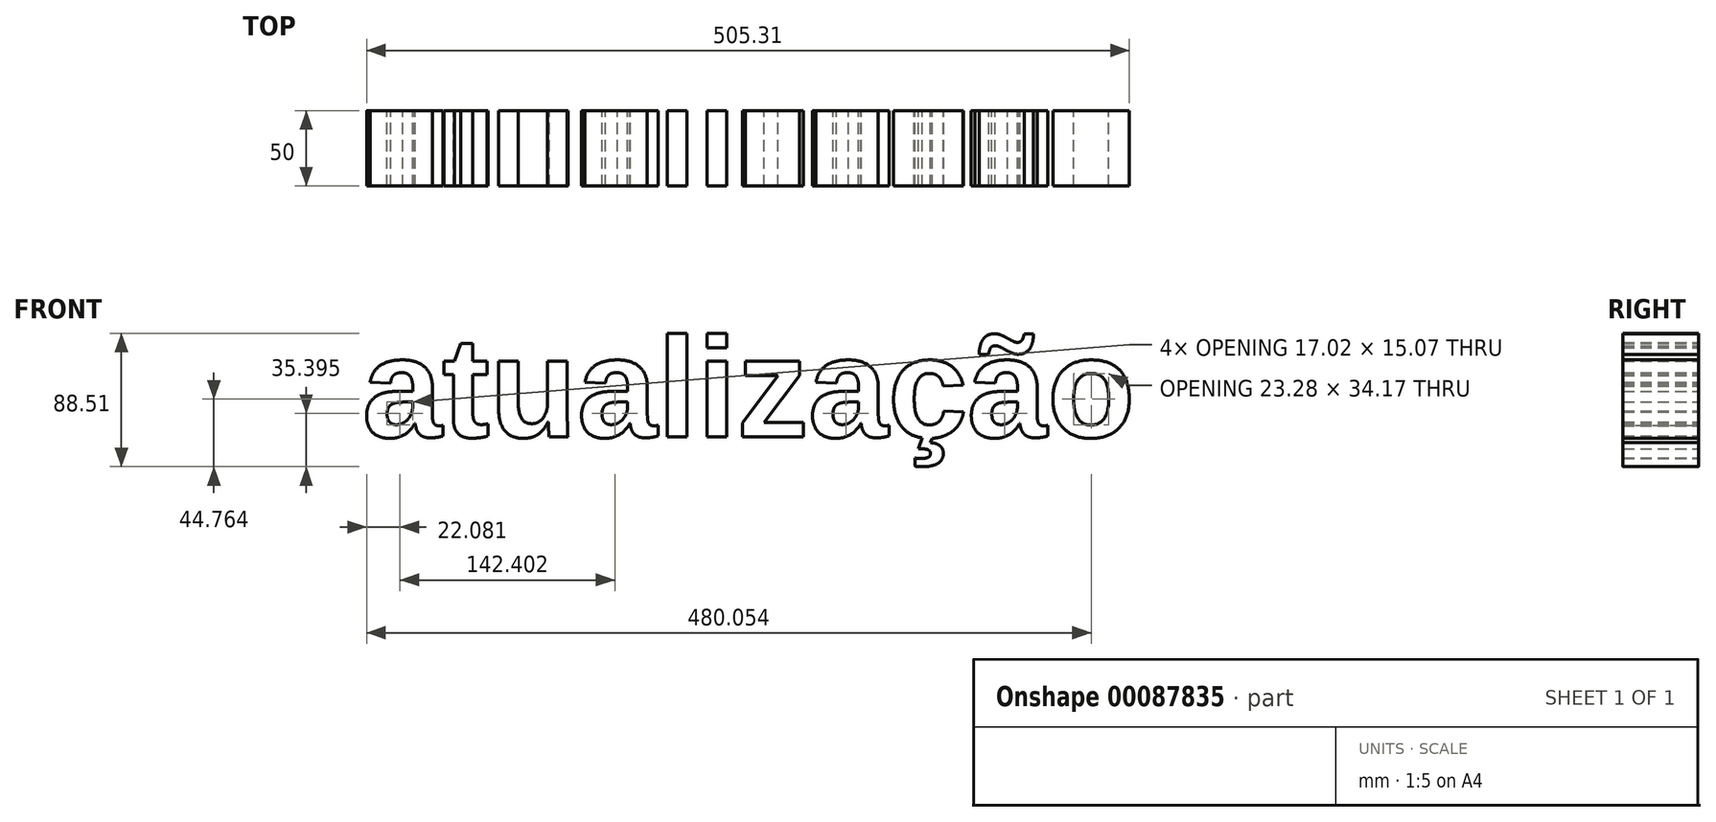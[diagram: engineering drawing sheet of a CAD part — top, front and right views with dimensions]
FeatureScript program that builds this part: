
annotation { "Feature Type Name" : "Feature", "Feature Type Description" : "" }
export const myFeature = defineFeature(function(context is Context, id is Id, definition is map)
    precondition{}
    {
        {
            var Q0;
            Q0=qCreatedBy(makeId("Front.planeOp"),FACE);
            var sketch = newSketch(context, id + "F0", { "sketchPlane" : qUnion([Q0])});
            skText(sketch, "E0", { "text": "atualização", "fontName": "Arimo-Bold.ttf"});
            const initialGuessF0  = {"E0": [-0.17746, -0.03606, 1, 0, 0.06836]};
            skSetInitialGuess(sketch, initialGuessF0);
            skSolve(sketch);
        }
        {
            var Q0;
            Q0 = qSketchRegion(id + "F0", true);
            extrude(context, id + "F1", {"entities" : qUnion([Q0]), "endBound" : BoundingType.SYMMETRIC, "depth" : 50 * mm});
        }
    });
